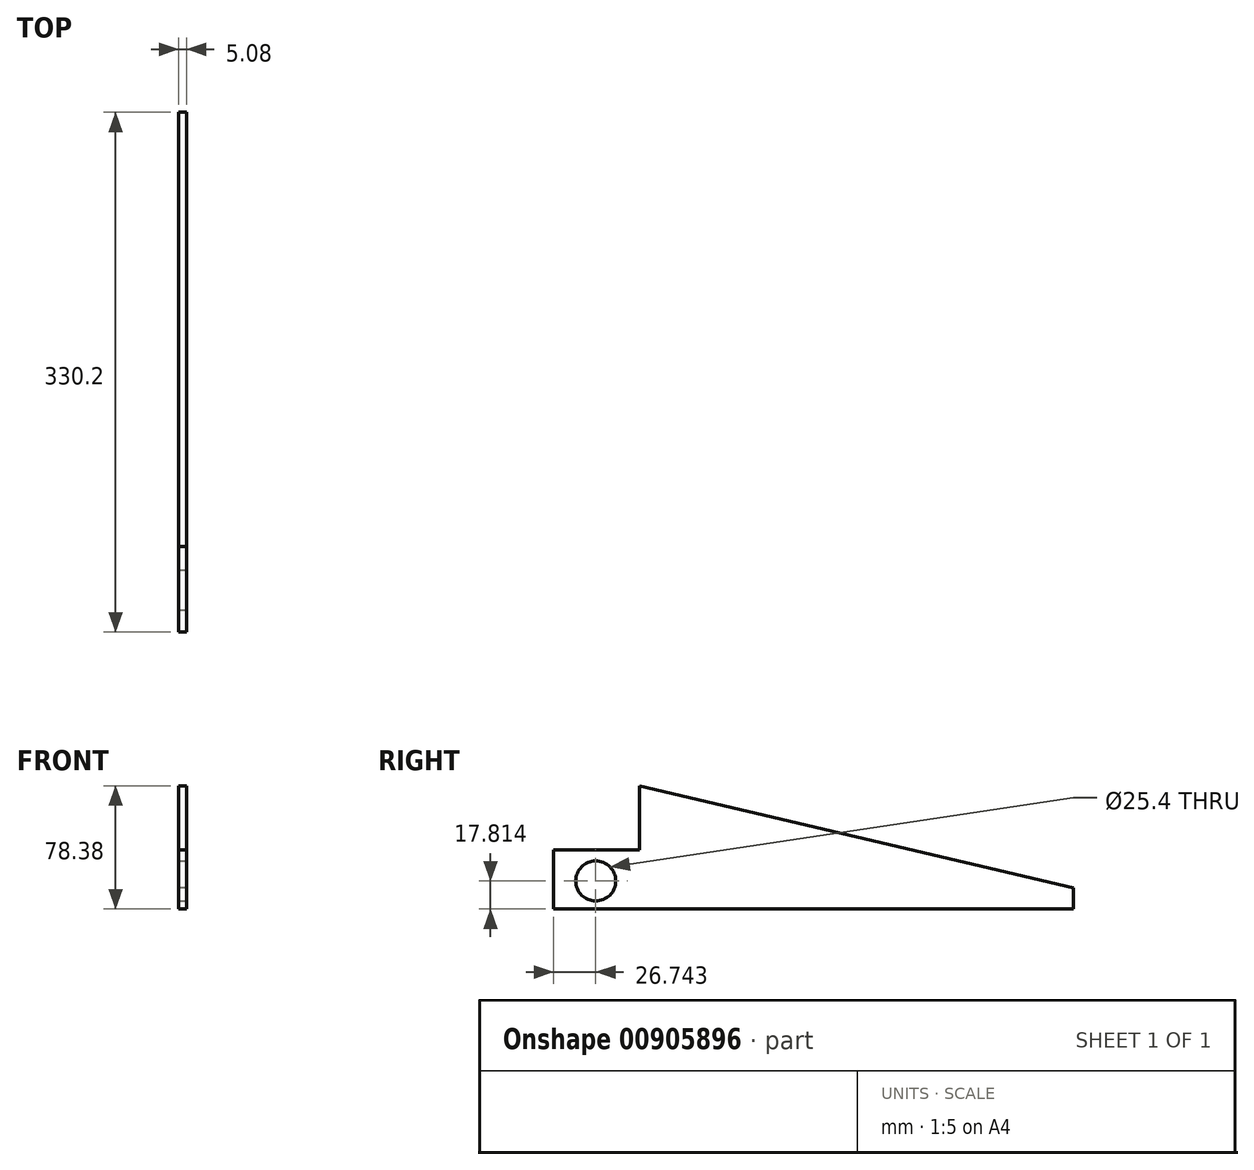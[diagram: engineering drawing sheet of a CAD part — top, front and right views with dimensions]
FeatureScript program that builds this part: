
annotation { "Feature Type Name" : "Feature", "Feature Type Description" : "" }
export const myFeature = defineFeature(function(context is Context, id is Id, definition is map)
    precondition{}
    {
        {
            var Q0;
            Q0=qCreatedBy(makeId("Right.planeOp"),FACE);
            var sketch = newSketch(context, id + "F0", { "sketchPlane" : qUnion([Q0])});
            skLineSegment(sketch, "E0", {"start": v(143.1, 13.62) * mm, "end": v(143.1, 0) * mm});
            skLineSegment(sketch, "E1", {"start": v(143.1, 0) * mm, "end": v(-132.54, 0) * mm});
            skLineSegment(sketch, "E2", {"start": v(-132.54, 0) * mm, "end": v(-187.1, 0) * mm});
            skLineSegment(sketch, "E3", {"start": v(-187.1, 0) * mm, "end": v(-187.1, 37.55) * mm});
            skLineSegment(sketch, "E4", {"start": v(-187.1, 37.55) * mm, "end": v(-132.54, 37.55) * mm});
            skLineSegment(sketch, "E5", {"start": v(-132.54, 37.55) * mm, "end": v(-132.54, 78.38) * mm});
            skLineSegment(sketch, "E6", {"start": v(-132.54, 78.38) * mm, "end": v(143.1, 13.62) * mm});
            skSolve(sketch);
        }
        {
            var Q0;
            Q0 = qSketchRegion(id + "F0", true);
            extrude(context, id + "F1", {"entities" : qUnion([Q0]), "depth" : 5.08 * mm, "offsetDistance" : 25.4 * mm});
        }
        {
            var Q0;
            Q0=makeQuery(id+"F1.opExtrude","CAP_FACE",FACE,{"disambiguationData":[OSD([sQuery(id+"F0.wireOp",EDGE,"yOloGWCt-nTtU-IvOG-IZY0-FIVagWPBcws4"),sQuery(id+"F0.wireOp",EDGE,"WTZwx11x-okz1-BqpJ-oY5s-NN6DVcVHIxSz"),sQuery(id+"F0.wireOp",EDGE,"E0"),sQuery(id+"F0.wireOp",EDGE,"E1"),sQuery(id+"F0.wireOp",EDGE,"c7qW6OyJ-ENbJ-aLQ8-qPPZ-AMWektXOuQ2y"),sQuery(id+"F0.wireOp",EDGE,"6FwH3hvA-k8OO-NWuX-mNoH-66ijBf5Wpp9w"),sQuery(id+"F0.wireOp",EDGE,"FltngxYj-49zW-u3c2-RIPA-KWbySyTjM0h3")])],"isStart":false});
            var sketch = newSketch(context, id + "F2", { "sketchPlane" : qUnion([Q0])});
            skCircle(sketch, "E7", {"center": v(-160.36, 17.81) * mm, "radius": 12.7 * mm});
            skSolve(sketch);
        }
        {
            var Q0;
            Q0 = qSketchRegion(id + "F2", true);
            var Q1;
            Q1=sQuery(id+"F2.wireOp",EDGE,"E7");
            extrude(context, id + "F3", {"entities" : qUnion([Q0]), "operationType" : NewBodyOperationType.REMOVE, "surfaceEntities" : qUnion([Q1]), "oppositeDirection" : true, "depth" : 12.7 * mm, "offsetDistance" : 25.4 * mm});
        }
    });
